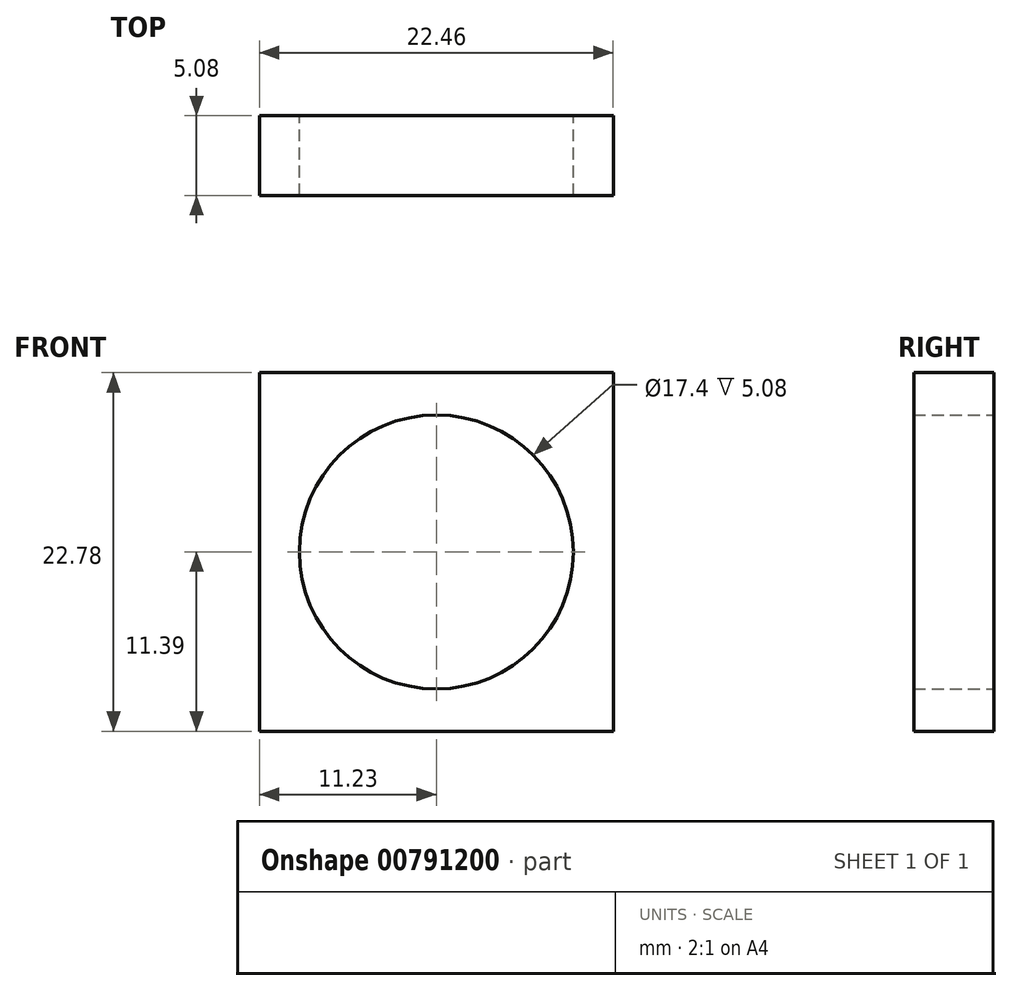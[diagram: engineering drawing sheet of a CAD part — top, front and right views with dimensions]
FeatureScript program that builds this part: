
annotation { "Feature Type Name" : "Feature", "Feature Type Description" : "" }
export const myFeature = defineFeature(function(context is Context, id is Id, definition is map)
    precondition{}
    {
        {
            var Q0;
            Q0=qCreatedBy(makeId("Front.planeOp"),FACE);
            var sketch = newSketch(context, id + "F0", { "sketchPlane" : qUnion([Q0])});
            skLineSegment(sketch, "E0.bottom", {"start": v(11.23, -11.39) * mm, "end": v(-11.23, -11.39) * mm});
            skLineSegment(sketch, "E0.top", {"start": v(11.23, 11.39) * mm, "end": v(-11.23, 11.39) * mm});
            skLineSegment(sketch, "E0.left", {"start": v(11.23, -11.39) * mm, "end": v(11.23, 11.39) * mm});
            skLineSegment(sketch, "E0.right", {"start": v(-11.23, -11.39) * mm, "end": v(-11.23, 11.39) * mm});
            skPoint(sketch, "E0.middle", {"position": v(0, 0) * mm});
            skCircle(sketch, "E1", {"center": v(0, 0) * mm, "radius": 8.7 * mm});
            skSolve(sketch);
        }
        {
            var Q0;
            Q0 = qSketchRegion(id + "F0", true);
            extrude(context, id + "F1", {"entities" : qUnion([Q0]), "depth" : 5.08 * mm, "offsetDistance" : 25.4 * mm});
        }
    });
